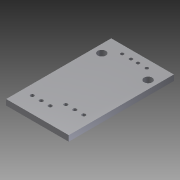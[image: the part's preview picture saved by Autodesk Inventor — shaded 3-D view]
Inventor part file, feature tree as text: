
AUTODESK INVENTOR PART (.ipt)
format: ipt  version: 2013 (Build 170138000, 138)  size: 88,064 bytes
history: native  units: mm
features: extrude x1, imported_body x1
ambient origin geometry x8: Origin, YZ Plane, XZ Plane, XY Plane, X Axis, Y Axis, Z Axis, Center Point
feature tree (2):
  extrude  "Extrude3"  [1 undecoded]
  imported_body  "Base1"
note: 1 required parameter value undecoded (feature->parameter linkage not recoverable at this tier; creation-order binding heuristic only, values carry confidence <= 0.55)
